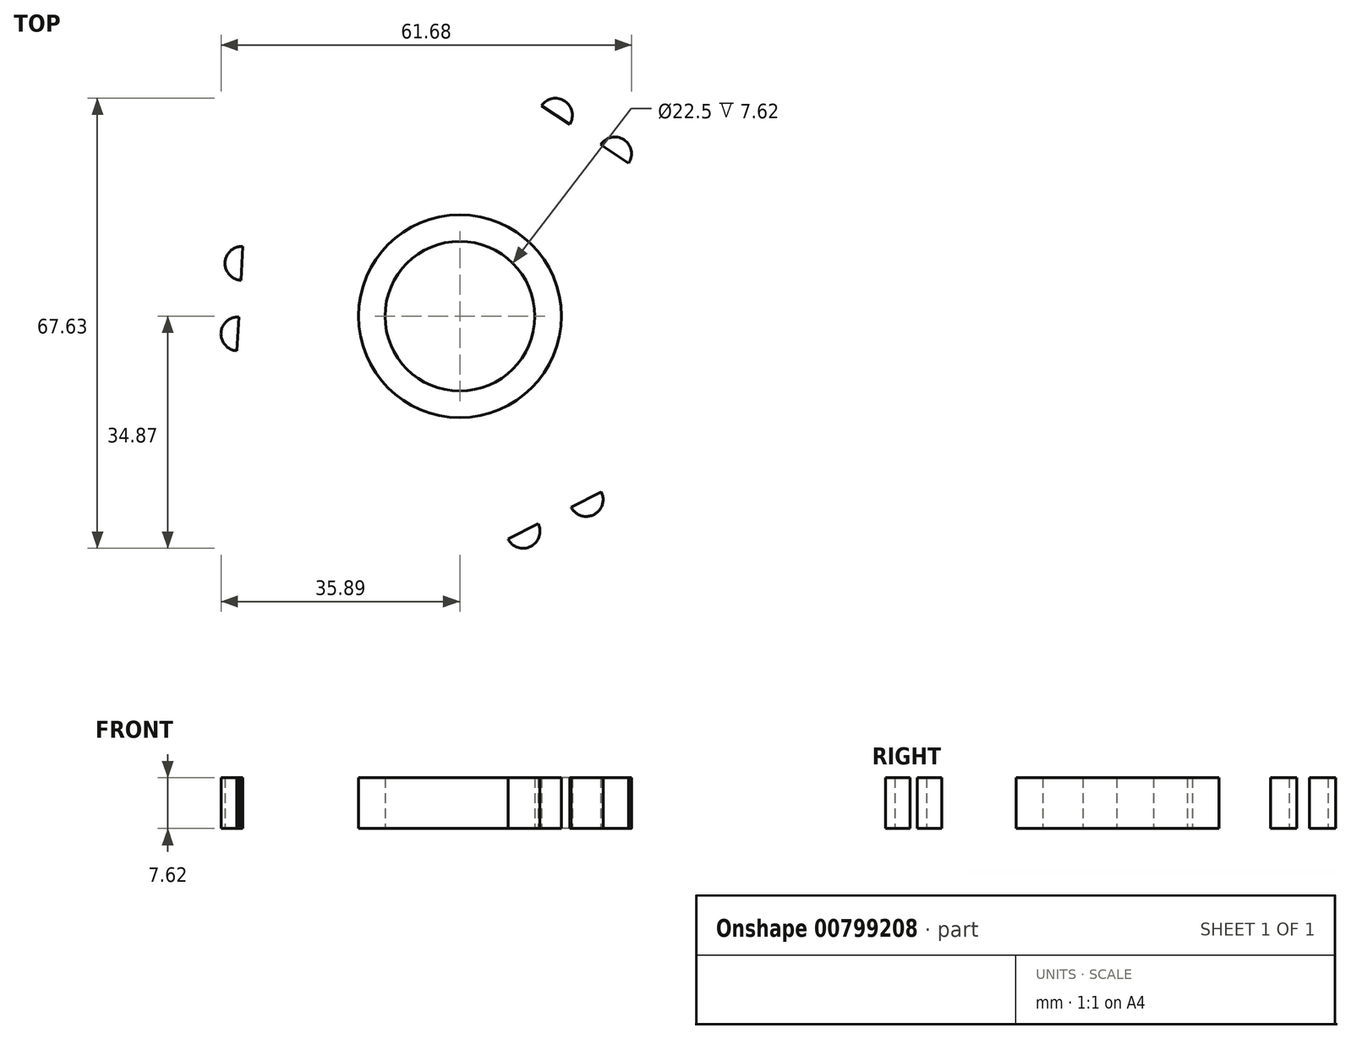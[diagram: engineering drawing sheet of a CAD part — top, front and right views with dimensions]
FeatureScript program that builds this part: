
annotation { "Feature Type Name" : "Feature", "Feature Type Description" : "" }
export const myFeature = defineFeature(function(context is Context, id is Id, definition is map)
    precondition{}
    {
        {
            var Q0;
            Q0=qCreatedBy(makeId("Top.planeOp"),FACE);
            var sketch = newSketch(context, id + "F0", { "sketchPlane" : qUnion([Q0])});
            skCircle(sketch, "E0", {"center": v(0, 0) * mm, "radius": 11.25 * mm});
            skCircle(sketch, "E1", {"center": v(0, 0) * mm, "radius": 15.24 * mm});
            skLineSegment(sketch, "E2", {"start": v(0, 15.24) * mm, "end": v(12.7, 15.24) * mm});
            skLineSegment(sketch, "E3", {"start": v(12.7, 15.24) * mm, "end": v(0, 15.24) * mm});
            skLineSegment(sketch, "E4", {"start": v(12.7, 15.24) * mm, "end": v(12.24, 17.74) * mm});
            skLineSegment(sketch, "E5", {"start": v(12.24, 17.74) * mm, "end": v(5.06, 17.74) * mm});
            skLineSegment(sketch, "E6", {"start": v(5.06, 17.74) * mm, "end": v(5.06, 22.82) * mm});
            skLineSegment(sketch, "E7", {"start": v(5.06, 22.82) * mm, "end": v(37.2, 15.24) * mm});
            skLineSegment(sketch, "E8", {"start": v(37.2, 15.24) * mm, "end": v(5.06, 36.33) * mm});
            skArc(sketch, "E9", {"start": v(5.06, 36.33) * mm, "mid": v(4.94, 46.98) * mm, "end": v(0, 56.41) * mm});
            skArc(sketch, "E10", {"start": v(16.5, 28.82) * mm, "mid": v(15.77, 32.34) * mm, "end": v(12.25, 31.6) * mm});
            skArc(sketch, "E11", {"start": v(25.38, 23) * mm, "mid": v(24.65, 26.51) * mm, "end": v(21.13, 25.78) * mm});
            skArc(sketch, "E12.MirrorCS", {"start": v(-5.06, 36.33) * mm, "mid": v(-4.94, 46.98) * mm, "end": v(0, 56.41) * mm});
            skLineSegment(sketch, "E13.MirrorCS", {"start": v(-37.2, 15.24) * mm, "end": v(-5.06, 36.33) * mm});
            skArc(sketch, "E14.MirrorCS", {"start": v(-16.5, 28.82) * mm, "mid": v(-15.77, 32.34) * mm, "end": v(-12.25, 31.6) * mm});
            skArc(sketch, "E15.MirrorCS", {"start": v(-25.38, 23) * mm, "mid": v(-24.65, 26.51) * mm, "end": v(-21.13, 25.78) * mm});
            skLineSegment(sketch, "E16.MirrorCS", {"start": v(-5.06, 22.82) * mm, "end": v(-37.2, 15.24) * mm});
            skLineSegment(sketch, "E17.MirrorCS", {"start": v(-5.06, 17.74) * mm, "end": v(-5.06, 22.82) * mm});
            skLineSegment(sketch, "E18.MirrorCS", {"start": v(-12.24, 17.74) * mm, "end": v(-5.06, 17.74) * mm});
            skLineSegment(sketch, "E19.MirrorCS", {"start": v(-12.7, 15.24) * mm, "end": v(-12.24, 17.74) * mm});
            skLineSegment(sketch, "E20.MirrorCS", {"start": v(-12.7, 15.24) * mm, "end": v(0, 15.24) * mm});
            skLineSegment(sketch, "E21.1.0", {"start": v(5.4, -39.83) * mm, "end": v(-28.93, -22.54) * mm});
            skLineSegment(sketch, "E21.1.1", {"start": v(-22.3, -7.03) * mm, "end": v(-31.8, 24.6) * mm});
            skArc(sketch, "E21.1.2", {"start": v(-28.93, -22.54) * mm, "mid": v(-38.21, -27.76) * mm, "end": v(-48.86, -28.2) * mm});
            skArc(sketch, "E21.1.3", {"start": v(-33.99, -13.78) * mm, "mid": v(-43.15, -19.21) * mm, "end": v(-48.86, -28.2) * mm});
            skLineSegment(sketch, "E21.1.4", {"start": v(-17.23, -15.8) * mm, "end": v(5.4, -39.83) * mm});
            skArc(sketch, "E21.1.5", {"start": v(-33.2, -0.13) * mm, "mid": v(-35.89, -2.52) * mm, "end": v(-33.5, -5.2) * mm});
            skLineSegment(sketch, "E21.1.6", {"start": v(-31.8, 24.6) * mm, "end": v(-33.99, -13.78) * mm});
            skArc(sketch, "E21.1.7", {"start": v(-7.23, -33.47) * mm, "mid": v(-10.64, -34.6) * mm, "end": v(-11.76, -31.19) * mm});
            skArc(sketch, "E21.1.8", {"start": v(-16.71, -28.7) * mm, "mid": v(-20.12, -29.82) * mm, "end": v(-21.25, -26.41) * mm});
            skLineSegment(sketch, "E21.1.9", {"start": v(-19.55, 3.38) * mm, "end": v(-13.2, -7.62) * mm});
            skLineSegment(sketch, "E21.1.10", {"start": v(-12.83, -13.25) * mm, "end": v(-17.23, -15.8) * mm});
            skArc(sketch, "E21.1.11", {"start": v(-32.6, 10.48) * mm, "mid": v(-35.28, 8.09) * mm, "end": v(-32.9, 5.4) * mm});
            skLineSegment(sketch, "E21.1.12", {"start": v(-17.9, -4.49) * mm, "end": v(-22.3, -7.03) * mm});
            skLineSegment(sketch, "E21.1.13", {"start": v(-21.48, 1.73) * mm, "end": v(-17.9, -4.49) * mm});
            skLineSegment(sketch, "E21.1.14", {"start": v(-6.85, -18.62) * mm, "end": v(-13.2, -7.62) * mm});
            skLineSegment(sketch, "E21.1.15", {"start": v(-9.24, -19.47) * mm, "end": v(-12.83, -13.25) * mm});
            skLineSegment(sketch, "E21.1.16", {"start": v(-6.85, -18.62) * mm, "end": v(-9.24, -19.47) * mm});
            skLineSegment(sketch, "E21.1.17", {"start": v(-19.55, 3.38) * mm, "end": v(-21.48, 1.73) * mm});
            skLineSegment(sketch, "E21.1.18", {"start": v(-13.2, -7.62) * mm, "end": v(-19.55, 3.38) * mm});
            skLineSegment(sketch, "E21.2.0", {"start": v(31.8, 24.6) * mm, "end": v(33.99, -13.78) * mm});
            skLineSegment(sketch, "E21.2.1", {"start": v(17.23, -15.8) * mm, "end": v(-5.4, -39.83) * mm});
            skArc(sketch, "E21.2.2", {"start": v(33.99, -13.78) * mm, "mid": v(43.15, -19.21) * mm, "end": v(48.86, -28.2) * mm});
            skArc(sketch, "E21.2.3", {"start": v(28.93, -22.54) * mm, "mid": v(38.21, -27.76) * mm, "end": v(48.86, -28.2) * mm});
            skLineSegment(sketch, "E21.2.4", {"start": v(22.3, -7.03) * mm, "end": v(31.8, 24.6) * mm});
            skArc(sketch, "E21.2.5", {"start": v(16.71, -28.7) * mm, "mid": v(20.12, -29.82) * mm, "end": v(21.25, -26.41) * mm});
            skLineSegment(sketch, "E21.2.6", {"start": v(-5.4, -39.83) * mm, "end": v(28.93, -22.54) * mm});
            skArc(sketch, "E21.2.7", {"start": v(32.6, 10.48) * mm, "mid": v(35.28, 8.09) * mm, "end": v(32.9, 5.4) * mm});
            skArc(sketch, "E21.2.8", {"start": v(33.2, -0.13) * mm, "mid": v(35.89, -2.52) * mm, "end": v(33.5, -5.2) * mm});
            skLineSegment(sketch, "E21.2.9", {"start": v(6.85, -18.62) * mm, "end": v(13.2, -7.62) * mm});
            skLineSegment(sketch, "E21.2.10", {"start": v(17.9, -4.49) * mm, "end": v(22.3, -7.03) * mm});
            skArc(sketch, "E21.2.11", {"start": v(7.23, -33.47) * mm, "mid": v(10.64, -34.6) * mm, "end": v(11.76, -31.19) * mm});
            skLineSegment(sketch, "E21.2.12", {"start": v(12.83, -13.25) * mm, "end": v(17.23, -15.8) * mm});
            skLineSegment(sketch, "E21.2.13", {"start": v(9.24, -19.47) * mm, "end": v(12.83, -13.25) * mm});
            skLineSegment(sketch, "E21.2.14", {"start": v(19.55, 3.38) * mm, "end": v(13.2, -7.62) * mm});
            skLineSegment(sketch, "E21.2.15", {"start": v(21.48, 1.73) * mm, "end": v(17.9, -4.49) * mm});
            skLineSegment(sketch, "E21.2.16", {"start": v(19.55, 3.38) * mm, "end": v(21.48, 1.73) * mm});
            skLineSegment(sketch, "E21.2.17", {"start": v(6.85, -18.62) * mm, "end": v(9.24, -19.47) * mm});
            skLineSegment(sketch, "E21.2.18", {"start": v(13.2, -7.62) * mm, "end": v(6.85, -18.62) * mm});
            skSolve(sketch);
        }
        {
            var Q0;
            Q0=makeQuery(id+"F0.imprint","IMPRINT",FACE,{"disambiguationData":[TD([[makeQuery(id+"F0.imprint","IMPRINT",EDGE,{"derivedFrom":sQuery(id+"F0.wireOp",EDGE,"E0")}),-1.0]])]});
            var Q1;
            {var subQ25=sQuery(id+"F0.wireOp",EDGE,"E21.2.2");Q1=makeQuery(id+"F0.imprint","IMPRINT",FACE,{"disambiguationData":[TD([[makeQuery(id+"F0.imprint","IMPRINT",EDGE,{"derivedFrom":subQ25}),-1.0]])]});}
            var Q2;
            Q2=makeQuery(id+"F0.imprint","IMPRINT",FACE,{"disambiguationData":[TD([[makeQuery(id+"F0.imprint","IMPRINT",EDGE,{"derivedFrom":sQuery(id+"F0.wireOp",EDGE,"E3")}),-1.0]])]});
            var Q3;
            {var subQ23=sQuery(id+"F0.wireOp",EDGE,"E21.1.2");Q3=makeQuery(id+"F0.imprint","IMPRINT",FACE,{"disambiguationData":[TD([[makeQuery(id+"F0.imprint","IMPRINT",EDGE,{"derivedFrom":subQ23}),-1.0]])]});}
            var Q4;
            {var subQ0=sQuery(id+"F0.wireOp",EDGE,"E21.1.5");Q4=makeQuery(id+"F0.imprint","IMPRINT",FACE,{"disambiguationData":[TD([[makeQuery(id+"F0.imprint","IMPRINT",EDGE,{"derivedFrom":subQ0}),1.0]])]});}
            var Q5;
            {var subQ0=sQuery(id+"F0.wireOp",EDGE,"E21.1.11");Q5=makeQuery(id+"F0.imprint","IMPRINT",FACE,{"disambiguationData":[TD([[makeQuery(id+"F0.imprint","IMPRINT",EDGE,{"derivedFrom":subQ0}),1.0]])]});}
            var Q6;
            {var subQ0=sQuery(id+"F0.wireOp",EDGE,"E15.MirrorCS");Q6=makeQuery(id+"F0.imprint","IMPRINT",FACE,{"disambiguationData":[TD([[makeQuery(id+"F0.imprint","IMPRINT",EDGE,{"derivedFrom":subQ0}),-1.0]])]});}
            var Q7;
            {var subQ0=sQuery(id+"F0.wireOp",EDGE,"E14.MirrorCS");Q7=makeQuery(id+"F0.imprint","IMPRINT",FACE,{"disambiguationData":[TD([[makeQuery(id+"F0.imprint","IMPRINT",EDGE,{"derivedFrom":subQ0}),-1.0]])]});}
            var Q8;
            {var subQ0=sQuery(id+"F0.wireOp",EDGE,"E10");Q8=makeQuery(id+"F0.imprint","IMPRINT",FACE,{"disambiguationData":[TD([[makeQuery(id+"F0.imprint","IMPRINT",EDGE,{"derivedFrom":subQ0}),1.0]])]});}
            var Q9;
            {var subQ0=sQuery(id+"F0.wireOp",EDGE,"E11");Q9=makeQuery(id+"F0.imprint","IMPRINT",FACE,{"disambiguationData":[TD([[makeQuery(id+"F0.imprint","IMPRINT",EDGE,{"derivedFrom":subQ0}),1.0]])]});}
            var Q10;
            {var subQ0=sQuery(id+"F0.wireOp",EDGE,"E21.2.7");Q10=makeQuery(id+"F0.imprint","IMPRINT",FACE,{"disambiguationData":[TD([[makeQuery(id+"F0.imprint","IMPRINT",EDGE,{"derivedFrom":subQ0}),-1.0]])]});}
            var Q11;
            {var subQ0=sQuery(id+"F0.wireOp",EDGE,"E21.2.8");Q11=makeQuery(id+"F0.imprint","IMPRINT",FACE,{"disambiguationData":[TD([[makeQuery(id+"F0.imprint","IMPRINT",EDGE,{"derivedFrom":subQ0}),-1.0]])]});}
            var Q12;
            {var subQ0=sQuery(id+"F0.wireOp",EDGE,"E21.2.11");Q12=makeQuery(id+"F0.imprint","IMPRINT",FACE,{"disambiguationData":[TD([[makeQuery(id+"F0.imprint","IMPRINT",EDGE,{"derivedFrom":subQ0}),1.0]])]});}
            var Q13;
            {var subQ0=sQuery(id+"F0.wireOp",EDGE,"E21.2.5");Q13=makeQuery(id+"F0.imprint","IMPRINT",FACE,{"disambiguationData":[TD([[makeQuery(id+"F0.imprint","IMPRINT",EDGE,{"derivedFrom":subQ0}),1.0]])]});}
            var Q14;
            {var subQ0=sQuery(id+"F0.wireOp",EDGE,"E21.1.8");Q14=makeQuery(id+"F0.imprint","IMPRINT",FACE,{"disambiguationData":[TD([[makeQuery(id+"F0.imprint","IMPRINT",EDGE,{"derivedFrom":subQ0}),-1.0]])]});}
            var Q15;
            {var subQ0=sQuery(id+"F0.wireOp",EDGE,"E21.1.7");Q15=makeQuery(id+"F0.imprint","IMPRINT",FACE,{"disambiguationData":[TD([[makeQuery(id+"F0.imprint","IMPRINT",EDGE,{"derivedFrom":subQ0}),-1.0]])]});}
            extrude(context, id + "F1", {"entities" : qUnion([Q0, Q1, Q2, Q3, Q4, Q5, Q6, Q7, Q8, Q9, Q10, Q11, Q12, Q13, Q14, Q15]), "depth" : 7.62 * mm, "offsetDistance" : 25.4 * mm});
        }
    });
